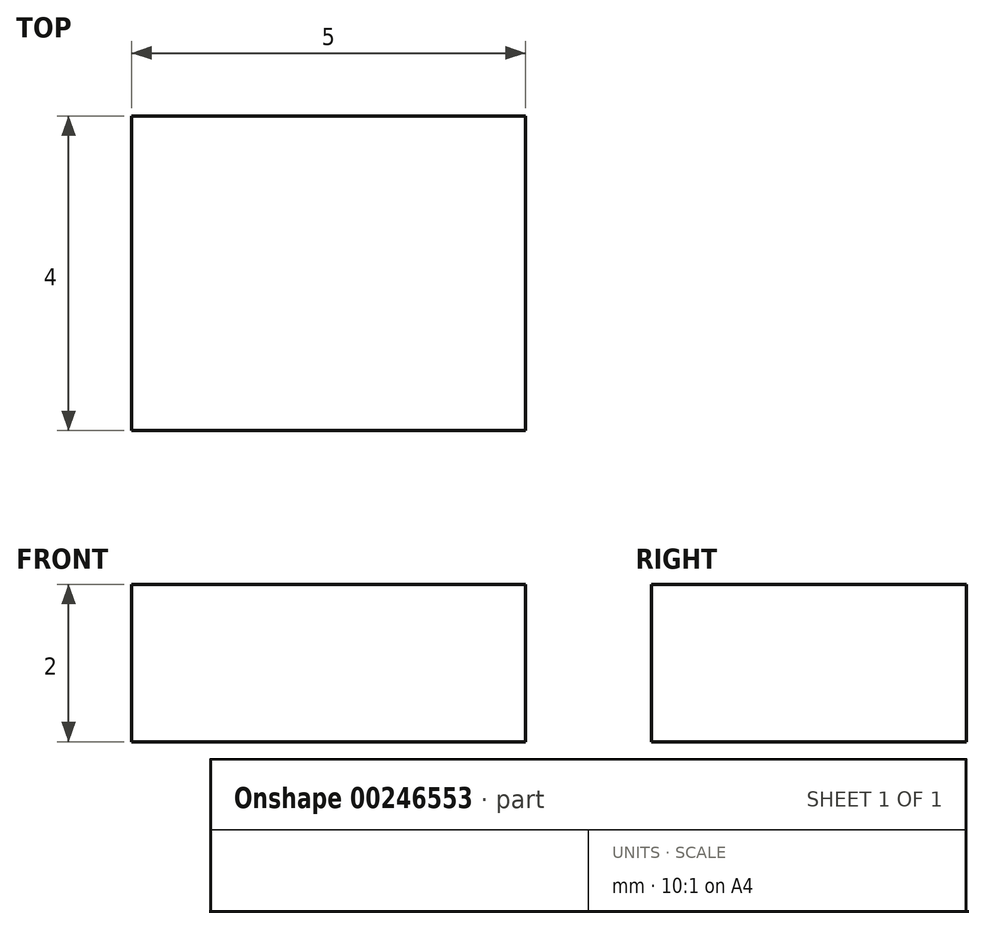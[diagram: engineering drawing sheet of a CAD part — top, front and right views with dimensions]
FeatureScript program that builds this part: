
annotation { "Feature Type Name" : "Feature", "Feature Type Description" : "" }
export const myFeature = defineFeature(function(context is Context, id is Id, definition is map)
    precondition{}
    {
        {
            var Q0;
            Q0=qCreatedBy(makeId("Top.planeOp"),FACE);
            var sketch = newSketch(context, id + "F0", { "sketchPlane" : qUnion([Q0])});
            skLineSegment(sketch, "E0.bottom", {"start": v(0, 4) * mm, "end": v(5, 4) * mm});
            skLineSegment(sketch, "E0.top", {"start": v(0, 0) * mm, "end": v(5, 0) * mm});
            skLineSegment(sketch, "E0.left", {"start": v(0, 4) * mm, "end": v(0, 0) * mm});
            skLineSegment(sketch, "E0.right", {"start": v(5, 4) * mm, "end": v(5, 0) * mm});
            skSolve(sketch);
        }
        {
            var Q0;
            Q0=makeQuery(id+"F0.imprint","IMPRINT",FACE,{"disambiguationData":[TD([[makeQuery(id+"F0.imprint","IMPRINT",EDGE,{"derivedFrom":sQuery(id+"F0.wireOp",EDGE,"E0.bottom")}),-1.0]])]});
            extrude(context, id + "F1", {"entities" : qUnion([Q0]), "depth" : 2 * mm});
        }
    });
